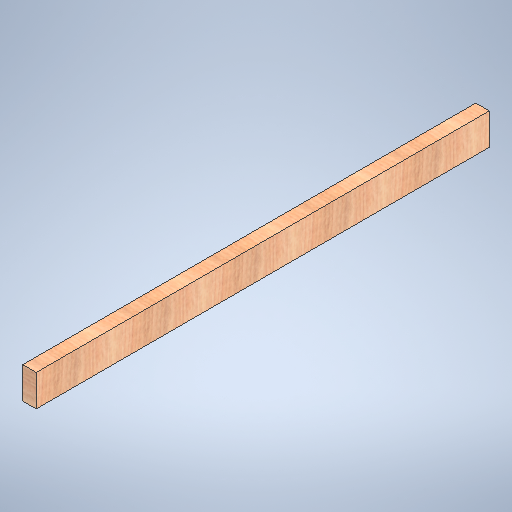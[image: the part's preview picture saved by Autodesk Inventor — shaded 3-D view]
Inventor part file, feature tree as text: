
AUTODESK INVENTOR PART (.ipt)
format: ipt  version: 2025 (Build 290162010, 162A)  size: 317,952 bytes
history: native  units: in
note: dims shown in document units (in); Inventor stores cm internally (conversion verified against a paired STEP export)
features: extrude x1, sketch x1
ambient origin geometry x8: Origin, YZ Plane, XZ Plane, XY Plane, X Axis, Y Axis, Z Axis, Center Point
bodies: Solid1 (feature_tree)
feature tree (2):
  extrude  "Extrusion1"  Depth=1.5in TaperAngle=0.0deg
  sketch  "Sketch1"  dims[d1=50.25in d2=1.5in d3=0.0in d4=3.5in]
